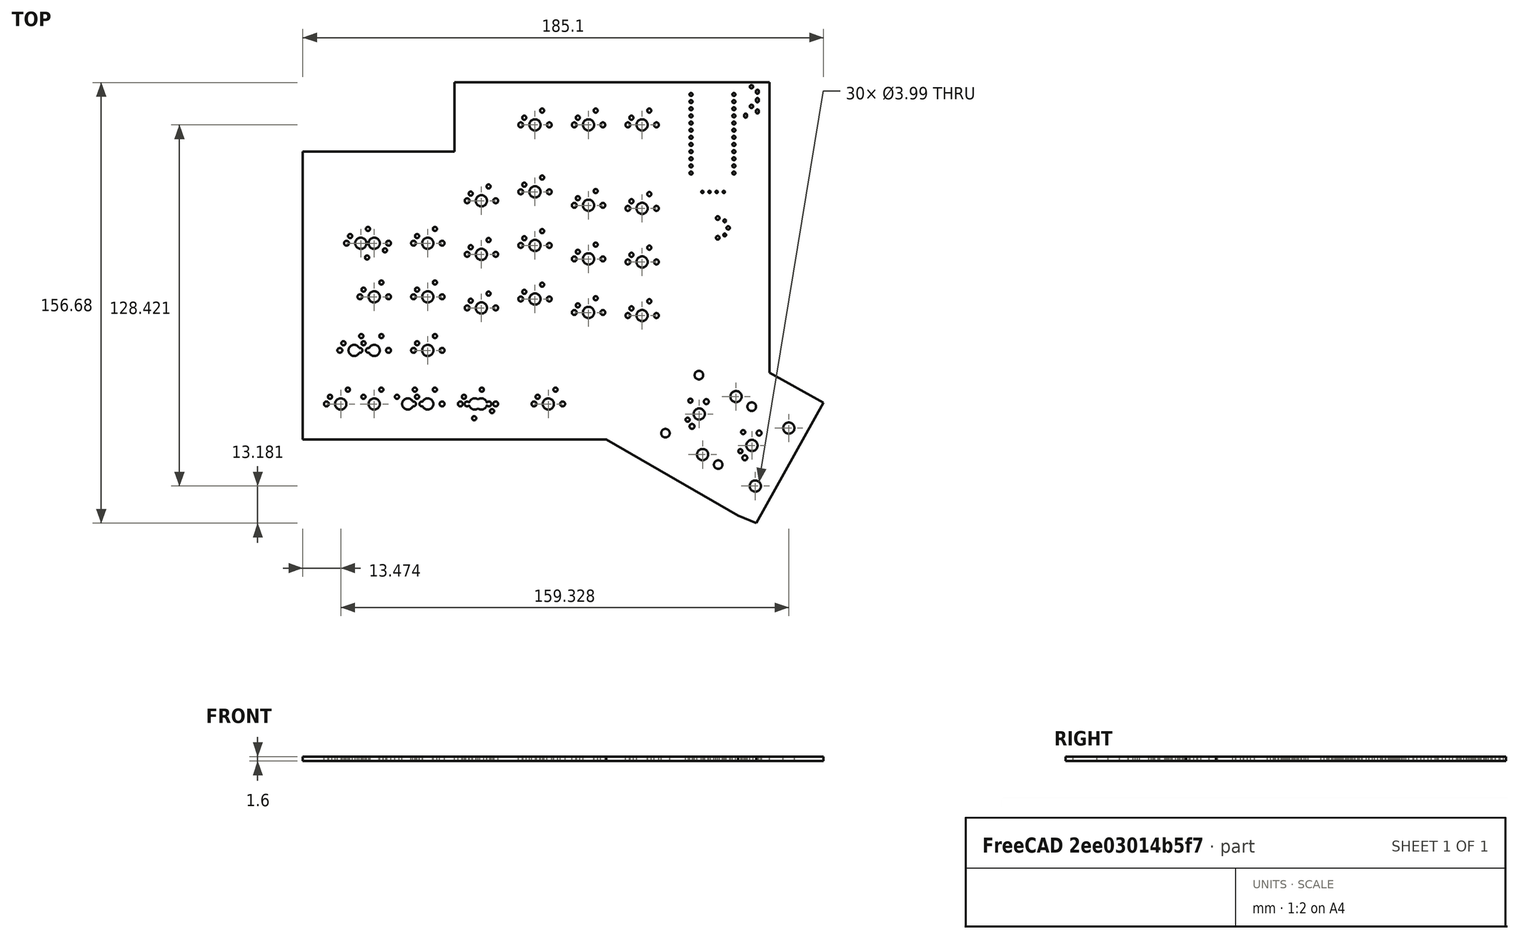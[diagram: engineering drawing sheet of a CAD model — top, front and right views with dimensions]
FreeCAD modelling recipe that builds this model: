
FCSTD DOCUMENT  (FreeCAD 0.19R14555 (Git shallow))
Label: left_case
License: All rights reserved
LicenseURL: http://en.wikipedia.org/wiki/All_rights_reserved
objects: Part::Feature×1, Sketcher::SketchObject×1, PartDesign::Body×1
note: 3 computed .brp shape members not serialized (recipe doc carries the construction recipe); baked Part::Feature solids carry a one-line shape summary decoded from their .brp

FEATURE [Part::Feature] Solid  label="bourbondox2_left pcb"
  shape: bbox 185.1 x 156.7 x 1.6 mm, 242 faces (baked)
FEATURE [Sketcher::SketchObject] Sketch
  FullyConstrained = false
  MapMode = 5
  Support = -> [XY_Plane]
  sketch-geometry (10):
    g0: LineSegment StartX=130.955 StartY=-11.2762 StartZ=0 EndX=260.266 EndY=-11.2762 EndZ=0
    g1: LineSegment StartX=262.342 StartY=-14.5387 StartZ=0 EndX=262.342 EndY=-113.598 EndZ=0
    g2: LineSegment StartX=271.24 StartY=-119.53 StartZ=0 EndX=295.857 EndY=-131.69 EndZ=0
    g3: LineSegment StartX=298.822 StartY=-138.808 StartZ=0 EndX=283.4 EndY=-167.576 EndZ=0
    g4: LineSegment StartX=220.524 StartY=-179.736 StartZ=0 EndX=193.831 EndY=-160.755 EndZ=0
    g5: LineSegment StartX=186.12 StartY=-156.899 StartZ=0 EndX=83.2053 EndY=-156.899 EndZ=0
    g6: LineSegment StartX=71.3419 StartY=-156.01 StartZ=0 EndX=71.3419 EndY=-45.0869 EndZ=0
    g7: LineSegment StartX=71.3419 StartY=-34.1132 StartZ=0 EndX=113.457 EndY=-34.1132 EndZ=0
    g8: LineSegment StartX=125.32 StartY=-33.2235 StartZ=0 EndX=125.32 EndY=-12.7591 EndZ=0
    g9: LineSegment StartX=138.101 StartY=-18.5546 StartZ=0 EndX=249.866 EndY=-18.5546 EndZ=0
  constraints (11):
    c: Horizontal(g0)
    c: Vertical(g1)
    c: Horizontal(g5)
    c: Vertical(g6)
    c: Horizontal(g7)
    c: Vertical(g8)
    c: Horizontal(g9)
    c: DistanceX(g9) = 138.101
    c: DistanceY(g9) = -18.5546
    c: DistanceX(g9) = 249.866
    c: DistanceY(g9) = -18.5546
FEATURE [PartDesign::Body] Body
  Group = -> [Sketch]
  Origin = -> Origin
